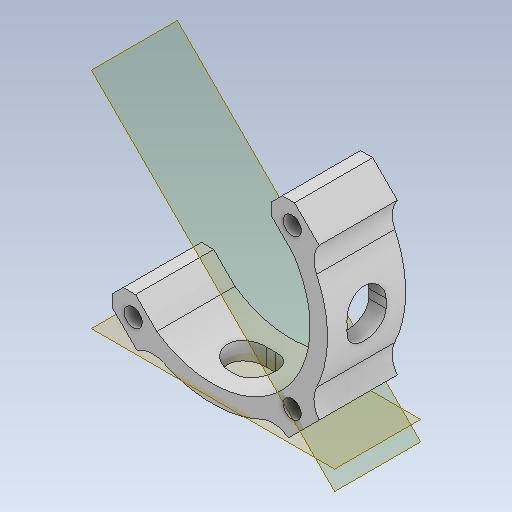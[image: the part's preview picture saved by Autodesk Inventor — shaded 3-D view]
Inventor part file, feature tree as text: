
AUTODESK INVENTOR PART (.ipt)
format: ipt  version: 2020 (Build 240168000, 168)  size: 358,400 bytes
history: native  units: mm
features: sketch x8, projected_geometry x7, extrude x6, plane x4, reference x4, other x4, thicken_offset x3, hole x2, fillet x1, mirror x1, chamfer x1
ambient origin geometry x8: Origin, YZ Plane, XZ Plane, XY Plane, X Axis, Y Axis, Z Axis, Center Point
bodies: Solid1 (feature_tree)
feature tree (41):
  sketch  "Sketch1"  dims[d0=45.0mm d1=4.0mm]
  plane  "Work Plane1"
  extrude  "Extrusion1"  Depth=4.0mm
  sketch  "Sketch2"  dims[d2=0.5mm d3=7.0mm]
  plane  "Work Plane2"
  extrude  "Extrusion2"  Depth=7.0mm
  thicken_offset  "Thicken1"
  thicken_offset  "Thicken2"
  hole  "Hole1"  [1 undecoded]
  hole  "Hole2"  [1 undecoded]
  extrude  "Extrusion5"  Depth=10.0mm
  extrude  "Extrusion6"  Depth=7.5mm
  extrude  "Extrusion7"  Depth=10.0mm
  fillet  "Fillet3"  Radius=10.0mm
  thicken_offset  "Thicken3"
  plane  "Work Plane6"
  plane  "Work Plane7"
  extrude  "Extrusion8"  Depth=7.5mm
  mirror  "Mirror3"
  chamfer  "Chamfer2"  Distance=10.0mm
  reference  "Reference1"
  reference  "Reference2"
  reference  "Reference3"
  reference  "Reference4"
  projected_geometry  "Projected Loop1"
  sketch  "Sketch3"  dims[d4=40.0mm d6=360.0deg d8=10.0mm d9=0.0mm]
  projected_geometry  "Projected Loop2"
  sketch  "Sketch4"  dims[d10=10.0mm d11=0.0mm d12=10.0mm]
  projected_geometry  "Projected Loop3"
  sketch  "Sketch8"  dims[d13=10.0mm d14=10.0mm]
  projected_geometry  "Projected Loop7"
  sketch  "Sketch9"  dims[d15=10.0mm]
  projected_geometry  "Projected Loop8"
  sketch  "Sketch10"  dims[d16=4.15mm d17=6.0mm d18=4.0mm d19=2.0mm d20=90.0deg d21=7.0mm d22=0.0mm]
  projected_geometry  "Projected Loop9"
  sketch  "Sketch11"  dims[d27=4.15mm d28=6.0mm d29=4.0mm d30=2.0mm d31=90.0deg d32=7.0mm d33=0.0mm d49=7.5mm d50=10.0mm d51=10.0mm d52=0.0mm d53=7.5mm d54=10.0mm d55=10.0mm d56=0.0mm d57=10.0mm d58=7.5mm d59=10.0mm d60=0.0mm d61=6.0mm d62=1.0mm d63=1.0mm d64=1.0mm d65=9.0mm d66=10.0mm d67=0.0mm d68=2.0mm d69=2.0mm d70=45.0deg]
  projected_geometry  "Projected Loop10"
  parser-record x1  (decoder bookkeeping rows leaked as tree rows — omitted from the tree; the rows remain in map.json)
  other  "reducer_1.iam"
  other  "motor_holder_4:1"
  other  "motor_holder_5:1"
note: 2 required parameter values undecoded (feature->parameter linkage not recoverable at this tier; creation-order binding heuristic only, values carry confidence <= 0.55)
note: 1 file-system path scrubbed to <path> (originals preserved in map.json)
